# Revit family: BTALU200
name_source: partatom
category: Structural Connections
revit_build: Autodesk Revit 2015 (Build: 20140606_1530(x64)
units: mm (PartAtom-declared; Revit-internal decimal feet)

## types (1)
- BTALU200
    Default Elevation = 0 mm  [stored 0 ft]
    Density = 0.51 kg
    Description = Concealed beam hanger
    EPD = https://www.strongtie.eu
    ETA / DoP = https://www.strongtie.eu
    H = 198.2 mm  [stored 0.650262 ft]
    Manufacturer = Simpson Strong-Tie
    Model = BTALU200
    Model Disclaimer = Contact Simpson Strong-Tie Company  for more information
    Model ID = 0157996627218539974592128131601238326215
    Name = BTALU200
    ObjectType = BTALU200
    Product Material = Galvanised
    Product Type = Concealed beam hanger
    Reference = BTALU200
    Technical datasheet = https://www.strongtie.eu
    URL = www.strongtie.eu
    UniClass Number = Pr_20_85_09_02
    UniClass Title = Aluminium brackets
    W = 62 mm  [stored 0.203412 ft]

note: [stored X ft] marks values corroborated as IEEE doubles in the binary element streams (Revit-internal decimal feet)

## geometry (parser evidence)
native form markers: Blend x29, Sweep x2
no freeform markers — native parametric forms only
